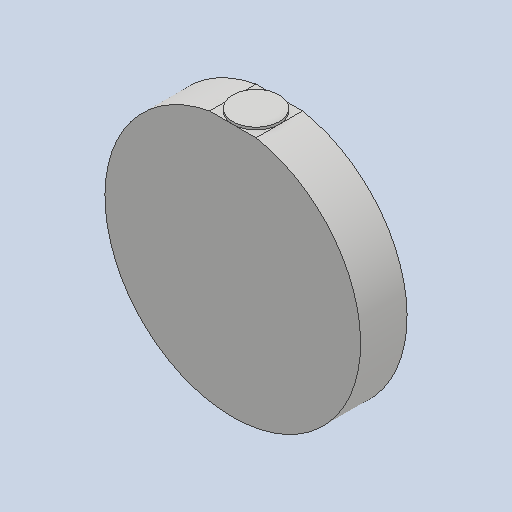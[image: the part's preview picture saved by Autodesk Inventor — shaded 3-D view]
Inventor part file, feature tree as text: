
AUTODESK INVENTOR PART (.ipt)
format: ipt  version: 2025 (Build 290162010, 162A)  size: 99,840 bytes
history: native  units: mm
features: extrude x2, sketch x2, other x1
ambient origin geometry x8: Origin, YZ Plane, XZ Plane, XY Plane, X Axis, Y Axis, Z Axis, Center Point
bodies: Body1 (feature_tree)
feature tree (5):
  other  "Твердое тело1"
  extrude  "Выдавливание1"  Depth=1.0mm TaperAngle=0.0deg
  extrude  "Выдавливание2"  Depth=55.0mm
  sketch  "Эскиз1"
  sketch  "Эскиз3"
